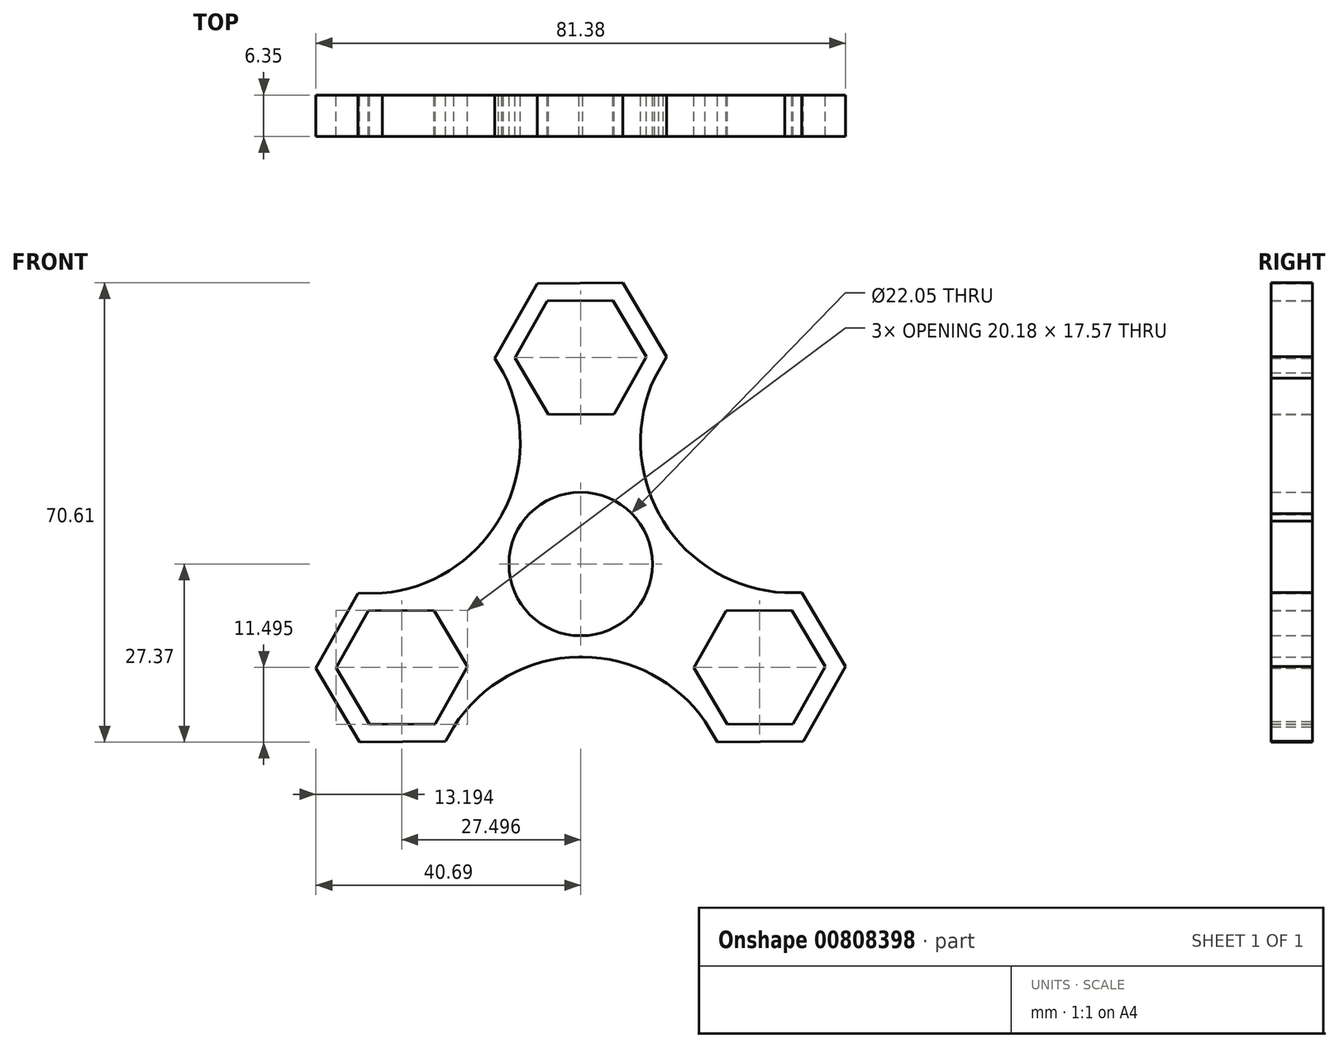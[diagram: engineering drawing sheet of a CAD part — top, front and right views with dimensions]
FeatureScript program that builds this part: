
annotation { "Feature Type Name" : "Feature", "Feature Type Description" : "" }
export const myFeature = defineFeature(function(context is Context, id is Id, definition is map)
    precondition{}
    {
        {
            var Q0;
            Q0=qCreatedBy(makeId("Front.planeOp"),FACE);
            var sketch = newSketch(context, id + "F0", { "sketchPlane" : qUnion([Q0])});
            skCircle(sketch, "E0", {"center": v(0, 0) * mm, "radius": 11.02 * mm});
            skCircle(sketch, "E1", {"center": v(0, 0) * mm, "radius": 14.29 * mm});
            skCircle(sketch, "E2.cCircle", {"center": v(0, 31.75) * mm, "radius": 11.43 * mm, "construction": true});
            skLineSegment(sketch, "E2.0", {"start": v(13.2, 31.87) * mm, "end": v(6.7, 20.38) * mm});
            skLineSegment(sketch, "E2.1", {"start": v(6.7, 20.38) * mm, "end": v(-6.5, 20.26) * mm});
            skLineSegment(sketch, "E2.2", {"start": v(-6.5, 20.26) * mm, "end": v(-13.2, 31.63) * mm});
            skLineSegment(sketch, "E2.3", {"start": v(-13.2, 31.63) * mm, "end": v(-6.7, 43.12) * mm});
            skLineSegment(sketch, "E2.4", {"start": v(-6.7, 43.12) * mm, "end": v(6.5, 43.24) * mm});
            skLineSegment(sketch, "E2.5", {"start": v(6.5, 43.24) * mm, "end": v(13.2, 31.87) * mm});
            skPoint(sketch, "E2.0.midPoint", {"position": v(9.95, 26.13) * mm});
            skCircle(sketch, "E3.cCircle", {"center": v(0, 31.75) * mm, "radius": 8.74 * mm, "construction": true});
            skLineSegment(sketch, "E3.0", {"start": v(-10.09, 31.66) * mm, "end": v(-5.13, 40.44) * mm});
            skLineSegment(sketch, "E3.1", {"start": v(-5.13, 40.44) * mm, "end": v(4.96, 40.53) * mm});
            skLineSegment(sketch, "E3.2", {"start": v(4.96, 40.53) * mm, "end": v(10.09, 31.84) * mm});
            skLineSegment(sketch, "E3.3", {"start": v(10.09, 31.84) * mm, "end": v(5.13, 23.06) * mm});
            skLineSegment(sketch, "E3.4", {"start": v(5.13, 23.06) * mm, "end": v(-4.96, 22.97) * mm});
            skLineSegment(sketch, "E3.5", {"start": v(-4.96, 22.97) * mm, "end": v(-10.09, 31.66) * mm});
            skPoint(sketch, "E3.0.midPoint", {"position": v(-7.6, 36.05) * mm});
            skCircle(sketch, "E4.1.0", {"center": v(-27.5, -15.87) * mm, "radius": 8.74 * mm, "construction": true});
            skLineSegment(sketch, "E4.1.1", {"start": v(-22.53, -7.1) * mm, "end": v(-17.4, -15.78) * mm});
            skLineSegment(sketch, "E4.1.2", {"start": v(-17.4, -15.78) * mm, "end": v(-22.37, -24.56) * mm});
            skLineSegment(sketch, "E4.1.3", {"start": v(-22.37, -24.56) * mm, "end": v(-32.46, -24.66) * mm});
            skLineSegment(sketch, "E4.1.4", {"start": v(-32.46, -24.66) * mm, "end": v(-37.59, -15.97) * mm});
            skLineSegment(sketch, "E4.1.5", {"start": v(-37.59, -15.97) * mm, "end": v(-32.62, -7.19) * mm});
            skLineSegment(sketch, "E4.1.6", {"start": v(-32.62, -7.19) * mm, "end": v(-22.53, -7.1) * mm});
            skLineSegment(sketch, "E4.1.7", {"start": v(-34.2, -4.5) * mm, "end": v(-21, -4.38) * mm});
            skCircle(sketch, "E4.1.8", {"center": v(-27.5, -15.87) * mm, "radius": 11.43 * mm, "construction": true});
            skLineSegment(sketch, "E4.1.9", {"start": v(-40.7, -16) * mm, "end": v(-34.2, -4.5) * mm});
            skLineSegment(sketch, "E4.1.10", {"start": v(-33.99, -27.37) * mm, "end": v(-40.7, -16) * mm});
            skLineSegment(sketch, "E4.1.11", {"start": v(-20.8, -27.24) * mm, "end": v(-33.99, -27.37) * mm});
            skLineSegment(sketch, "E4.1.12", {"start": v(-14.3, -15.75) * mm, "end": v(-20.8, -27.24) * mm});
            skLineSegment(sketch, "E4.1.13", {"start": v(-21, -4.38) * mm, "end": v(-14.3, -15.75) * mm});
            skCircle(sketch, "E4.2.0", {"center": v(27.5, -15.88) * mm, "radius": 8.74 * mm, "construction": true});
            skLineSegment(sketch, "E4.2.1", {"start": v(17.4, -15.97) * mm, "end": v(22.37, -7.19) * mm});
            skLineSegment(sketch, "E4.2.2", {"start": v(22.37, -7.19) * mm, "end": v(32.46, -7.1) * mm});
            skLineSegment(sketch, "E4.2.3", {"start": v(32.46, -7.1) * mm, "end": v(37.59, -15.78) * mm});
            skLineSegment(sketch, "E4.2.4", {"start": v(37.59, -15.78) * mm, "end": v(32.62, -24.56) * mm});
            skLineSegment(sketch, "E4.2.5", {"start": v(32.62, -24.56) * mm, "end": v(22.53, -24.66) * mm});
            skLineSegment(sketch, "E4.2.6", {"start": v(22.53, -24.66) * mm, "end": v(17.4, -15.97) * mm});
            skLineSegment(sketch, "E4.2.7", {"start": v(21, -27.37) * mm, "end": v(14.3, -16) * mm});
            skCircle(sketch, "E4.2.8", {"center": v(27.5, -15.88) * mm, "radius": 11.43 * mm, "construction": true});
            skLineSegment(sketch, "E4.2.9", {"start": v(34.2, -27.24) * mm, "end": v(21, -27.37) * mm});
            skLineSegment(sketch, "E4.2.10", {"start": v(40.7, -15.75) * mm, "end": v(34.2, -27.24) * mm});
            skLineSegment(sketch, "E4.2.11", {"start": v(33.99, -4.38) * mm, "end": v(40.7, -15.75) * mm});
            skLineSegment(sketch, "E4.2.12", {"start": v(20.8, -4.5) * mm, "end": v(33.99, -4.38) * mm});
            skLineSegment(sketch, "E4.2.13", {"start": v(14.3, -16) * mm, "end": v(20.8, -4.5) * mm});
            skArc(sketch, "E5", {"start": v(-34.2, -4.5) * mm, "mid": v(-12.43, 7) * mm, "end": v(-13.2, 31.63) * mm});
            skArc(sketch, "E6", {"start": v(21, -27.37) * mm, "mid": v(0.15, -14.28) * mm, "end": v(-20.8, -27.24) * mm});
            skArc(sketch, "E7", {"start": v(13.2, 31.87) * mm, "mid": v(12.28, 7.26) * mm, "end": v(33.99, -4.38) * mm});
            skSolve(sketch);
        }
        {
            var Q0;
            Q0=qSketchRegion(id+"F0",true);
            extrude(context, id + "F1", {"entities" : qUnion([Q0]), "depth" : 6.35 * mm, "offsetDistance" : 25.4 * mm});
        }
    });
